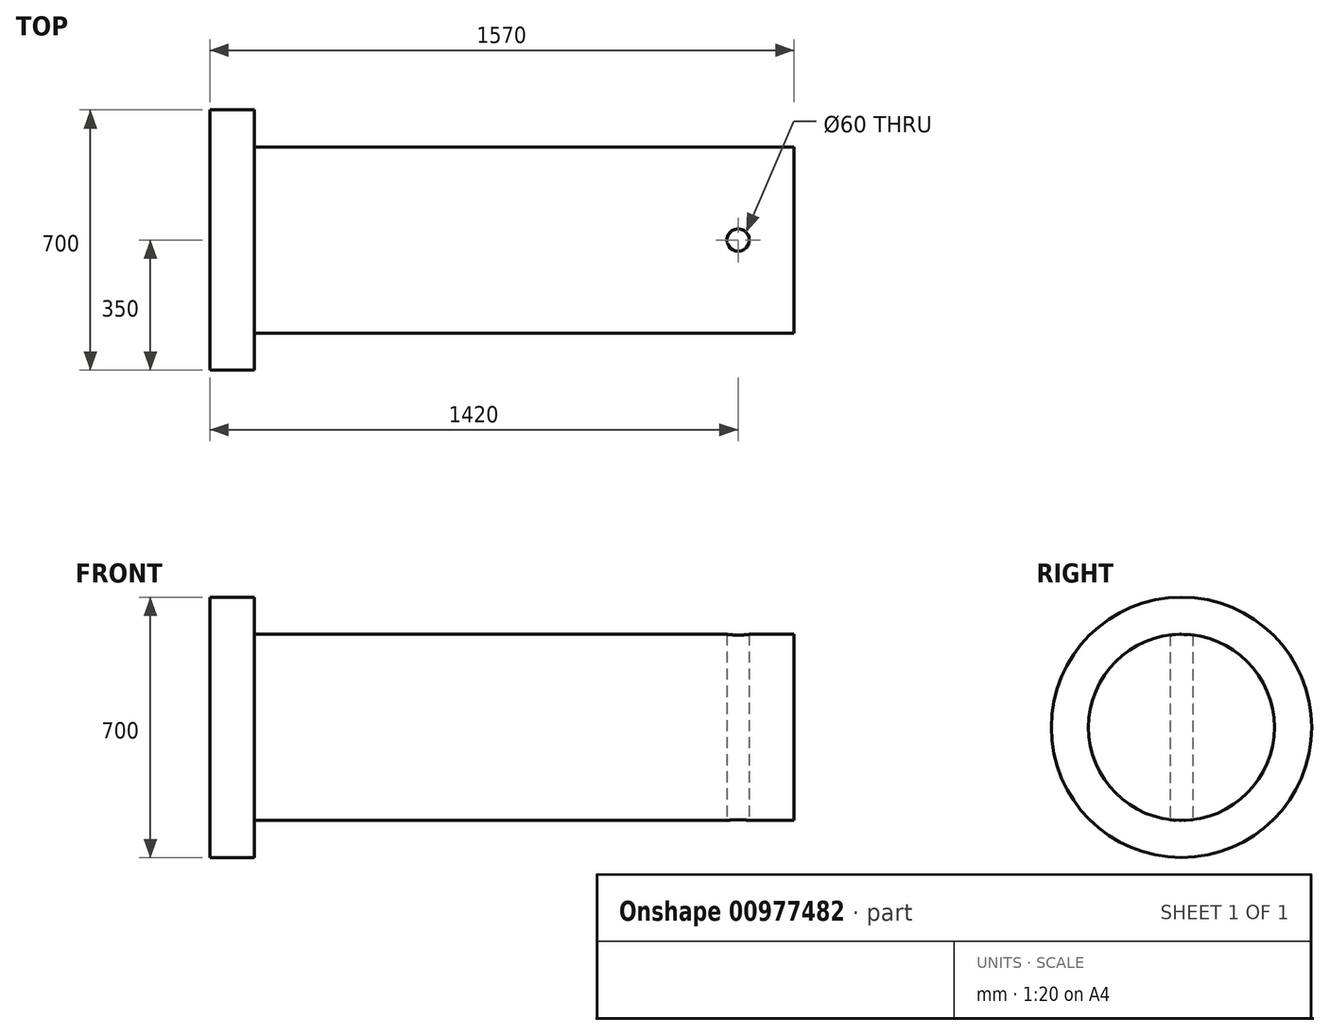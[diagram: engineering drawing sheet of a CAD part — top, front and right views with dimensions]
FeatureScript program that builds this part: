
annotation { "Feature Type Name" : "Feature", "Feature Type Description" : "" }
export const myFeature = defineFeature(function(context is Context, id is Id, definition is map)
    precondition{}
    {
        {
            var Q0;
            Q0=qCreatedBy(makeId("Front.planeOp"),FACE);
            var sketch = newSketch(context, id + "F0", { "sketchPlane" : qUnion([Q0])});
            skLineSegment(sketch, "E0", {"start": v(0, 0) * mm, "end": v(0, 250) * mm});
            skLineSegment(sketch, "E1", {"start": v(0, 250) * mm, "end": v(-1450, 250) * mm});
            skLineSegment(sketch, "E2", {"start": v(-1450, 250) * mm, "end": v(-1450, 350) * mm});
            skLineSegment(sketch, "E3", {"start": v(-1450, 350) * mm, "end": v(-1570, 350) * mm});
            skLineSegment(sketch, "E4", {"start": v(-1570, 350) * mm, "end": v(-1570, 0) * mm});
            skLineSegment(sketch, "E5", {"start": v(-1570, 0) * mm, "end": v(0, 0) * mm});
            skSolve(sketch);
        }
        {
            var Q0;
            Q0 = qSketchRegion(id + "F0", true);
            var Q1;
            Q1=sQuery(id+"F0.wireOp",EDGE,"E5");
            revolve(context, id + "F1", {"surfaceOperationType" : NewSurfaceOperationType.NEW, "entities" : qUnion([Q0]), "axis" : qUnion([Q1]), "revolveType" : RevolveType.FULL});
        }
        {
            var Q0;
            Q0=qCreatedBy(makeId("Top.planeOp"),FACE);
            var sketch = newSketch(context, id + "F2", { "sketchPlane" : qUnion([Q0])});
            skCircle(sketch, "E6", {"center": v(-150, 0) * mm, "radius": 30 * mm});
            skSolve(sketch);
        }
        {
            var Q0;
            Q0 = qSketchRegion(id + "F2", true);
            extrude(context, id + "F3", {"entities" : qUnion([Q0]), "operationType" : NewBodyOperationType.REMOVE, "endBound" : BoundingType.SYMMETRIC, "depth" : 1000 * mm, "offsetDistance" : 25 * mm});
        }
    });
